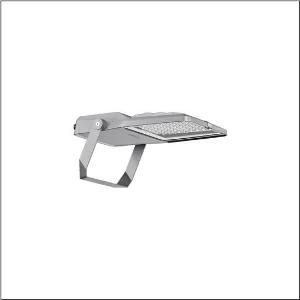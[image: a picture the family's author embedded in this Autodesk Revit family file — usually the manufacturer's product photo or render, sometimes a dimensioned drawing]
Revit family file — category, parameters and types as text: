
# Revit family: floodlight_fl_21_mini___pl43_5xa7773c4a1a_b3c2
name_source: partatom
category: Lighting Fixtures
units: mm (PartAtom-declared; Revit-internal decimal feet)

## family parameters
Cut with Voids When Loaded = No
Host = Face
Light Source = No
Part Type = Normal
Room Calculation Point = No
Round Connector Dimension = Use Diameter
Shared = No

## types (1)
- --- (1 x LED, 20890 lm, 163.5 W, 4000K)
    Apparent Load = 163 VA
    CIE Flux Codes = 27 78 99 100 100
    Color Rendering = 70
    Color Temperature = 4000K
    Default Elevation = 1800 mm
    Description = Floodlight FL 21 mini, floodlight, primary light control with lens, of PMMA, primary optical cover: protective disc, of toughened safety glass, transparent, light distribution: PL43, light emission: direct distribution, installation type: surface-mounted, LED, High Power LED, rated luminous flux: 20.890lm, luminous efficacy: 128lm/W, light colour: 740, colour temperature: 4000K, control: Temp-Guard, with terminal, 6-pole, mains connection: 220..240V, AC, 50/60Hz, start of lifetime: 164W, luminaire housing, of diecast aluminium, powder-coated, Siteco® metallic grey (DB 702S), corrosivity category C5 mid according to DIN EN ISO 12944, sealing non-destructively replaceable, mounting bracket, of steel, galvanised, powder-coated, Siteco® metallic grey (DB 702S), ON/OFF, protection rating (complete): IP66, insulation class (complete): insulation class I (protective earthing), certification: CE, ENEC, VDE, protection symbol: D, impact resistance: IK08, permissible operating ambient temperature: -40..+40°C, permissible operating ambient temperature for outdoor applications: -40..+50°C, standard: DIN EN 12944, LABS conformity tested according to VDMA 24364:2018-05, packaging unit: 1 piece

Light Distribution: PL43
    Height = 70 mm
    Lamp = 1 x LED
    Lamp Light Flux = 20890 lm
    Lamp Power = 163.5 W
    Lamp count = 1
    Length = 485 mm
    Luminous efficacy = 128 lm/W
    Manufacturer = Siteco
    ModVariant = No
    Model = 5XA7773C4A1A
    Number of Poles = 1
    OnlyDefault = Yes
    Power Factor = 1
    Product Name = Floodlight FL 21 mini | PL43
    Product group = floodlight | pylon annexe
    ProductGroupID = 6200
    Protection Class = Protection class I
    Protection Degree = IP 66
    RLX_Detail_Level = 1
    RLX_Emergency_Light_Flux = 0 lm
    RLX_Emergency_Type = 0
    RLX_Emergency_Type_DB = No
    RlxData = <blob elided: 94169 chars, md5=850e231c>
    Socket = socket
    Standby Power = 0 W
    System Light Flux = 20890 lm
    System Power = 163 W
    Type Comments = factory setting: luminous flux: 100 % | (ON | - | - | - | - | - | - | -) | 825 mA
    Type Image = l_1006845.jpg
    URL = http://relux.com
    VarID = @adj_093999
    Voltage = 0 V
    Weight = 0.00 kg
    Width = 337 mm

## geometry (parser evidence)
native form markers: Blend x4, Sweep x13
no freeform markers — native parametric forms only
